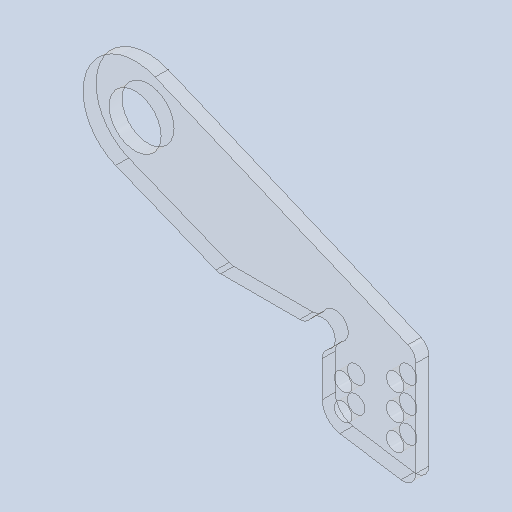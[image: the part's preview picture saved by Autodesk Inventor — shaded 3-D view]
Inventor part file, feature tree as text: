
AUTODESK INVENTOR PART (.ipt)
format: ipt  version: 2023 (Build 270158000, 158)  size: 137,728 bytes
history: native  units: in
note: dims shown in document units (in); Inventor stores cm internally (conversion verified against a paired STEP export)
features: other x3, extrude x1, fillet x1, sketch x1, reference x1
ambient origin geometry x8: Origin, YZ Plane, XZ Plane, XY Plane, X Axis, Y Axis, Z Axis, Center Point
bodies: Solid1 (feature_tree)
feature tree (7):
  extrude  "Extrusion1"  Depth=0.125in
  fillet  "Fillet1"  Radius=4.5in
  sketch  "Sketch1"  dims[d3=0.5in d4=2.0in d5=4.5in d6=1.8in d8=1.0in d10=0.25in d12=0.06in d13=1.0in d14=0.125in d15=0.0in d16=0.125in]
  reference  "Reference1"
  other  "<userpath>\Documents\CAD\spin-up-18_1\MainAssy.iam"
  other  "MainAssy.iam"
  other  "IntakeArm:2"
